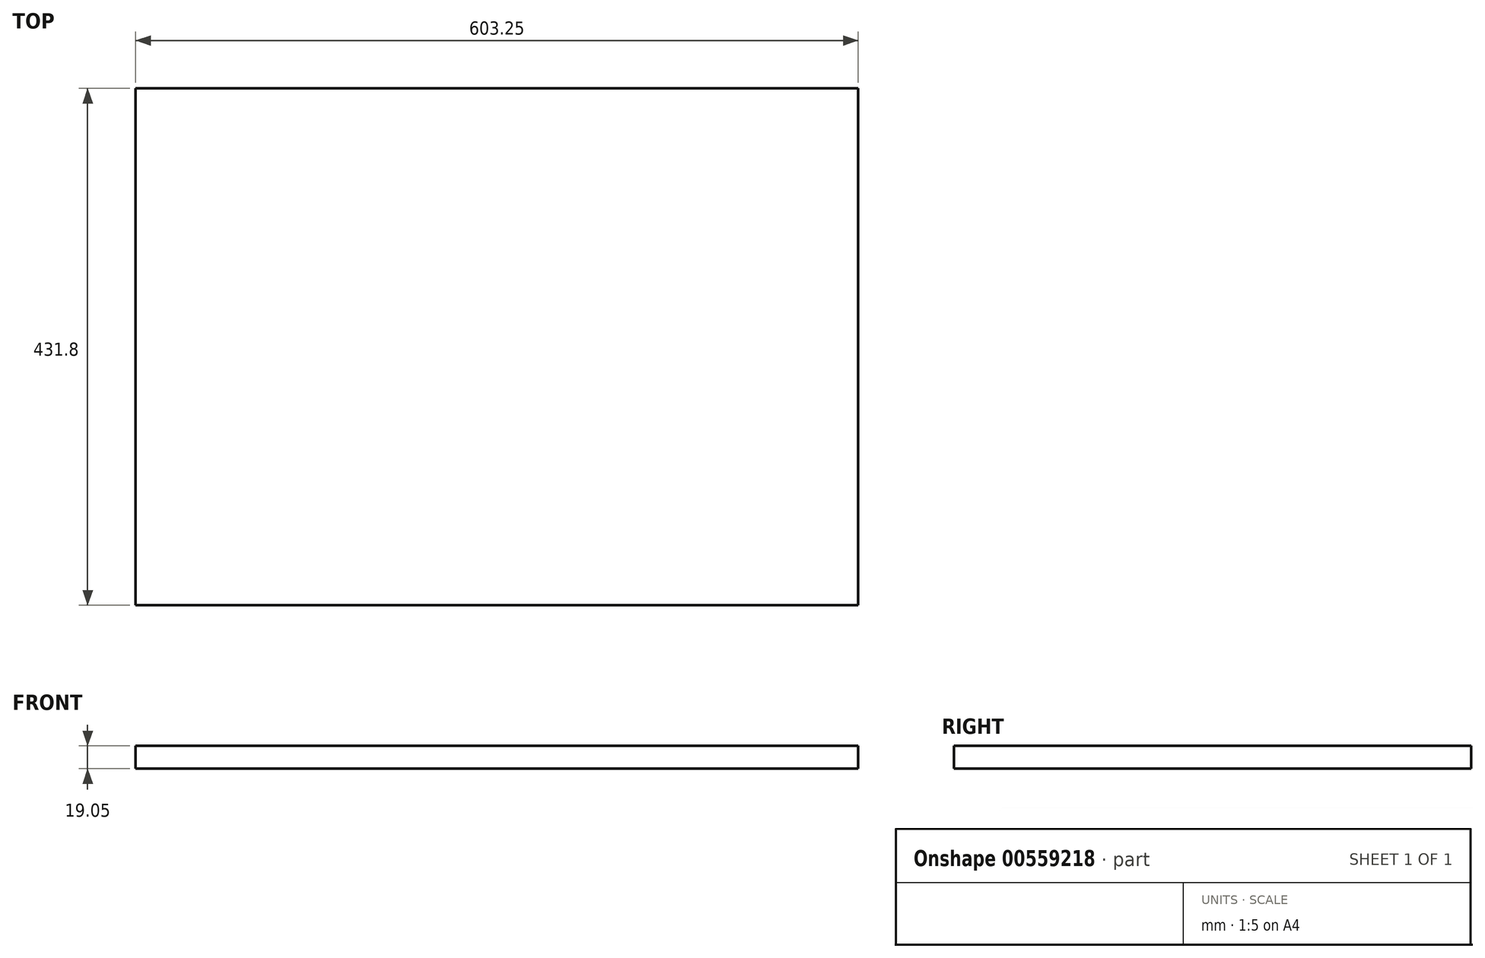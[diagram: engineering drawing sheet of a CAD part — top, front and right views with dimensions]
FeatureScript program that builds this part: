
annotation { "Feature Type Name" : "Feature", "Feature Type Description" : "" }
export const myFeature = defineFeature(function(context is Context, id is Id, definition is map)
    precondition{}
    {
        {
            var Q0;
            Q0=qCreatedBy(makeId("Top.planeOp"),FACE);
            var sketch = newSketch(context, id + "F0", { "sketchPlane" : qUnion([Q0])});
            skLineSegment(sketch, "E0.bottom", {"start": v(0, 0) * mm, "end": v(603.25, 0) * mm});
            skLineSegment(sketch, "E0.top", {"start": v(0, 431.8) * mm, "end": v(603.25, 431.8) * mm});
            skLineSegment(sketch, "E0.left", {"start": v(0, 0) * mm, "end": v(0, 431.8) * mm});
            skLineSegment(sketch, "E0.right", {"start": v(603.25, 0) * mm, "end": v(603.25, 431.8) * mm});
            skSolve(sketch);
        }
        {
            var Q0;
            Q0=makeQuery(id+"F0.imprint","IMPRINT",FACE,{"disambiguationData":[TD([[makeQuery(id+"F0.imprint","IMPRINT",EDGE,{"derivedFrom":sQuery(id+"F0.wireOp",EDGE,"E0.bottom")}),1.0]])]});
            extrude(context, id + "F1", {"entities" : qUnion([Q0]), "depth" : 19.05 * mm, "offsetDistance" : 25.4 * mm});
        }
    });
